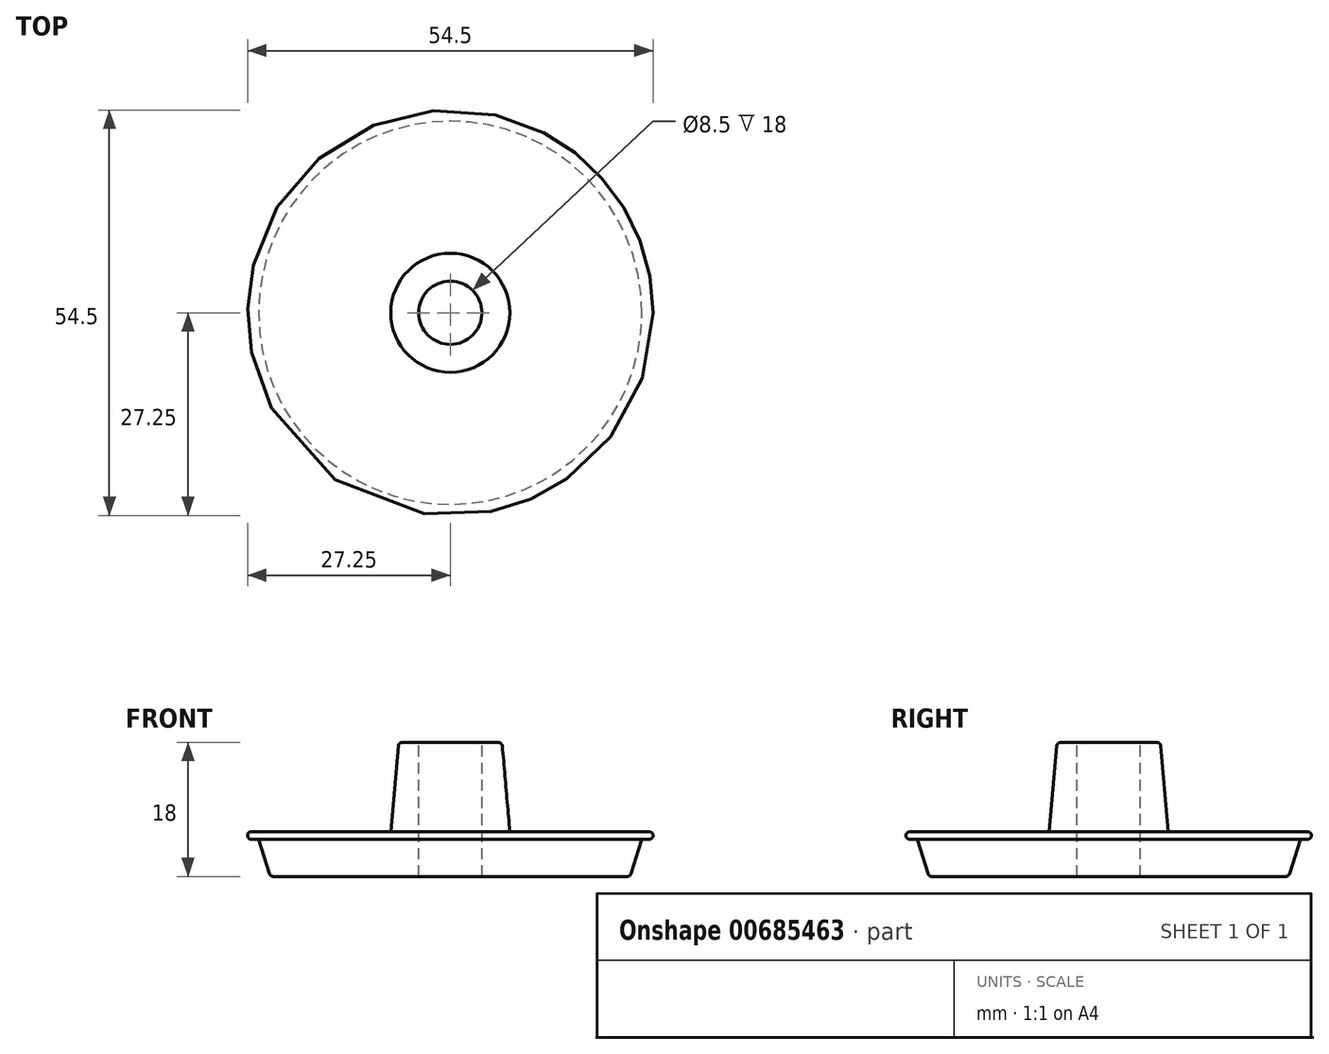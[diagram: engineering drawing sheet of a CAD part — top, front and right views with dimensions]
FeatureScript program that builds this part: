
annotation { "Feature Type Name" : "Feature", "Feature Type Description" : "" }
export const myFeature = defineFeature(function(context is Context, id is Id, definition is map)
    precondition{}
    {
        {
            var Q0;
            Q0=qCreatedBy(makeId("Top.planeOp"),FACE);
            var sketch = newSketch(context, id + "F0", { "sketchPlane" : qUnion([Q0])});
            skCircle(sketch, "E0", {"center": v(0, 0) * mm, "radius": 27.25 * mm});
            skCircle(sketch, "E1", {"center": v(0, 0) * mm, "radius": 25.75 * mm});
            skCircle(sketch, "E2", {"center": v(0, 0) * mm, "radius": 24.25 * mm});
            skSolve(sketch);
        }
        {
            var Q0;
            Q0=qSketchRegion(id+"F0",true);
            var Q1;
            Q1=makeQuery(id+"F0.imprint","IMPRINT",FACE,{"disambiguationData":[TD([[makeQuery(id+"F0.imprint","IMPRINT",EDGE,{"derivedFrom":sQuery(id+"F0.wireOp",EDGE,"E1")}),1.0]])]});
            var Q2;
            Q2=makeQuery(id+"F0.imprint","IMPRINT",FACE,{"disambiguationData":[TD([[makeQuery(id+"F0.imprint","IMPRINT",EDGE,{"derivedFrom":sQuery(id+"F0.wireOp",EDGE,"E2")}),1.0]])]});
            extrude(context, id + "F1", {"entities" : qUnion([Q0, Q1, Q2]), "depth" : 1 * mm});
        }
        {
            var Q0;
            Q0=makeQuery(id+"F0.imprint","IMPRINT",FACE,{"disambiguationData":[TD([[makeQuery(id+"F0.imprint","IMPRINT",EDGE,{"derivedFrom":sQuery(id+"F0.wireOp",EDGE,"E1")}),1.0]])]});
            var Q1;
            Q1=makeQuery(id+"F0.imprint","IMPRINT",FACE,{"disambiguationData":[TD([[makeQuery(id+"F0.imprint","IMPRINT",EDGE,{"derivedFrom":sQuery(id+"F0.wireOp",EDGE,"E2")}),1.0]])]});
            extrude(context, id + "F2", {"entities" : qUnion([Q0, Q1]), "operationType" : NewBodyOperationType.ADD, "oppositeDirection" : true, "depth" : 5 * mm, "hasDraft" : true, "draftAngle" : 17.5 * degree, "draftPullDirection" : true});
        }
        {
            var Q0;
            Q0=makeQuery(id+"F1.opExtrude","CAP_FACE",FACE,{"disambiguationData":[OSD([sQuery(id+"F0.wireOp",EDGE,"E0")])],"isStart":false});
            var sketch = newSketch(context, id + "F3", { "sketchPlane" : qUnion([Q0])});
            skCircle(sketch, "E3", {"center": v(0, 0) * mm, "radius": 8 * mm});
            skSolve(sketch);
        }
        {
            var Q0;
            Q0=makeQuery(id+"F3.imprint","IMPRINT",FACE,{"disambiguationData":[TD([[makeQuery(id+"F3.imprint","IMPRINT",EDGE,{"derivedFrom":sQuery(id+"F3.wireOp",EDGE,"E3")}),1.0]])]});
            extrude(context, id + "F4", {"entities" : qUnion([Q0]), "operationType" : NewBodyOperationType.ADD, "depth" : 12 * mm, "hasDraft" : true, "draftAngle" : 5 * degree, "draftPullDirection" : true});
        }
        {
            var Q0;
            Q0=makeQuery(id+"F4.opExtrude","CAP_FACE",FACE,{"disambiguationData":[OSD([sQuery(id+"F3.wireOp",EDGE,"E3")])],"isStart":false});
            var sketch = newSketch(context, id + "F5", { "sketchPlane" : qUnion([Q0])});
            skCircle(sketch, "E4", {"center": v(0, 0) * mm, "radius": 4.25 * mm});
            skSolve(sketch);
        }
        {
            var Q0;
            Q0=qSketchRegion(id+"F5",true);
            extrude(context, id + "F6", {"entities" : qUnion([Q0]), "operationType" : NewBodyOperationType.REMOVE, "endBound" : BoundingType.UP_TO_NEXT, "oppositeDirection" : true, "depth" : 25 * mm});
        }
        {
            var Q0;
            Q0=makeQuery(id+"F2.opExtrude","CAP_EDGE",EDGE,{"disambiguationData":[OSD([sQuery(id+"F0.wireOp",EDGE,"E1")])],"isStart":false});
            var Q1;
            Q1=makeQuery(id+"F1.opExtrude","CAP_EDGE",EDGE,{"disambiguationData":[OSD([sQuery(id+"F0.wireOp",EDGE,"E0")])],"isStart":true});
            var Q2;
            Q2=makeQuery(id+"F1.opExtrude","CAP_EDGE",EDGE,{"disambiguationData":[OSD([sQuery(id+"F0.wireOp",EDGE,"E0")])],"isStart":false});
            var Q3;
            Q3=makeQuery(id+"F6.boolean.opBoolean","COPY",EDGE,{"derivedFrom":makeQuery(id+"F6.opExtrude","CAP_EDGE",EDGE,{"disambiguationData":[OSD([sQuery(id+"F5.wireOp",EDGE,"E4")])],"isStart":false})});
            var Q4;
            Q4=makeQuery(id+"F4.opExtrude","CAP_EDGE",EDGE,{"disambiguationData":[OSD([sQuery(id+"F3.wireOp",EDGE,"E3")])],"isStart":true});
            var Q5;
            Q5=makeQuery(id+"F4.opExtrude","CAP_EDGE",EDGE,{"disambiguationData":[OSD([sQuery(id+"F3.wireOp",EDGE,"E3")])],"isStart":false});
            var Q6;
            Q6=makeQuery(id+"F6.boolean.opBoolean","COPY",EDGE,{"derivedFrom":makeQuery(id+"F6.opExtrude","CAP_EDGE",EDGE,{"disambiguationData":[OSD([sQuery(id+"F5.wireOp",EDGE,"E4")])],"isStart":true})});
            fillet(context, id + "F7", {"entities" : qUnion([Q0, Q1, Q2, Q3, Q4, Q5, Q6]), "radius" : .5 * mm, "tangentPropagation" : true, "allowEdgeOverflow" : false});
        }
    });
